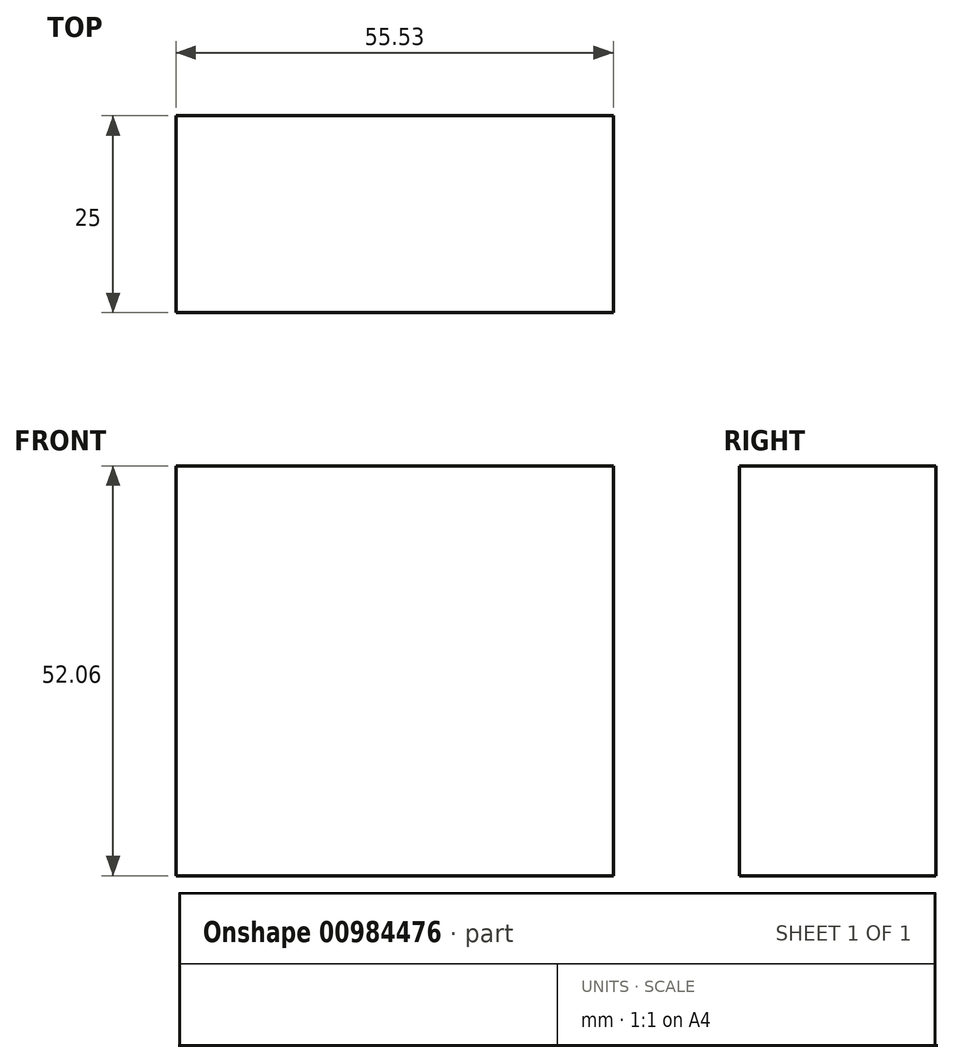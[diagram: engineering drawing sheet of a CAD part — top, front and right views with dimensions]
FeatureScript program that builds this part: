
annotation { "Feature Type Name" : "Feature", "Feature Type Description" : "" }
export const myFeature = defineFeature(function(context is Context, id is Id, definition is map)
    precondition{}
    {
        {
            var Q0;
            Q0=qCreatedBy(makeId("Front.planeOp"),FACE);
            var sketch = newSketch(context, id + "F0", { "sketchPlane" : qUnion([Q0])});
            skLineSegment(sketch, "E0.bottom", {"start": v(-90.45, 58.5) * mm, "end": v(-34.92, 58.5) * mm});
            skLineSegment(sketch, "E0.top", {"start": v(-90.45, 6.43) * mm, "end": v(-34.92, 6.43) * mm});
            skLineSegment(sketch, "E0.left", {"start": v(-90.45, 58.5) * mm, "end": v(-90.45, 6.43) * mm});
            skLineSegment(sketch, "E0.right", {"start": v(-34.92, 58.5) * mm, "end": v(-34.92, 6.43) * mm});
            skSolve(sketch);
        }
        {
            var Q0;
            Q0 = qSketchRegion(id + "F0", true);
            extrude(context, id + "F1", {"entities" : qUnion([Q0]), "depth" : 25 * mm, "offsetDistance" : 25 * mm});
        }
    });
